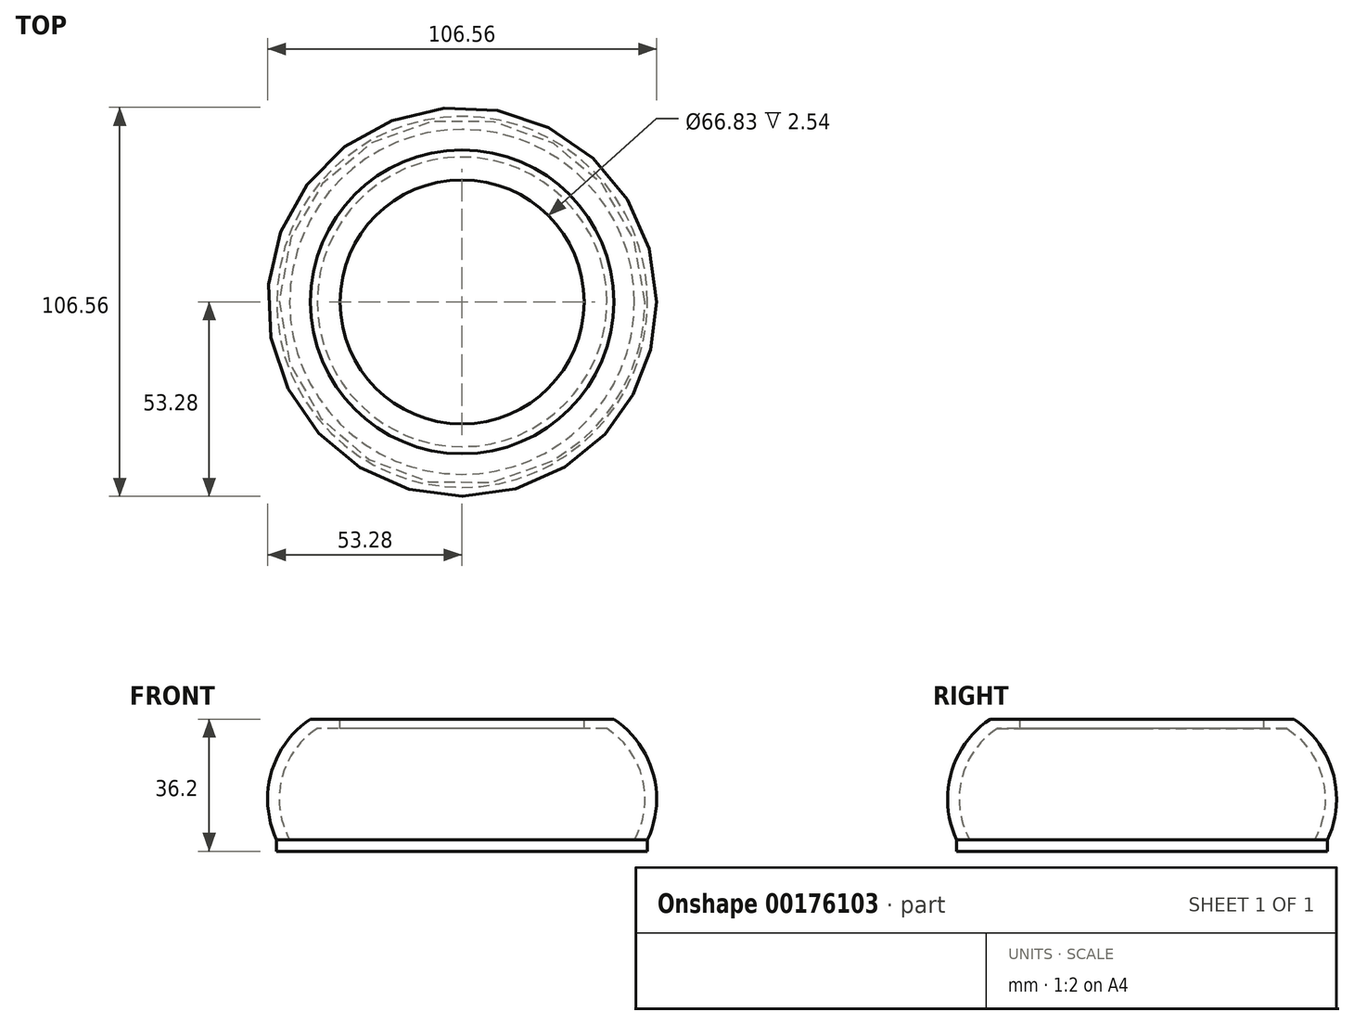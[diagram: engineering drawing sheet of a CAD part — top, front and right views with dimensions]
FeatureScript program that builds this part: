
annotation { "Feature Type Name" : "Feature", "Feature Type Description" : "" }
export const myFeature = defineFeature(function(context is Context, id is Id, definition is map)
    precondition{}
    {
        {
            var Q0;
            Q0=qCreatedBy(makeId("Front.planeOp"),FACE);
            var sketch = newSketch(context, id + "F0", { "sketchPlane" : qUnion([Q0])});
            skLineSegment(sketch, "E0", {"start": v(0, 0) * mm, "end": v(50.8, 0) * mm});
            skLineSegment(sketch, "E1", {"start": v(50.8, 0) * mm, "end": v(50.8, 3.18) * mm});
            skLineSegment(sketch, "E2", {"start": v(50.8, 3.18) * mm, "end": v(0, 3.17) * mm});
            skLineSegment(sketch, "E3", {"start": v(0, 3.17) * mm, "end": v(0, 0) * mm});
            skArc(sketch, "E4", {"start": v(50.8, 3.17) * mm, "mid": v(52.31, 21.4) * mm, "end": v(41.58, 36.2) * mm});
            skArc(sketch, "E5.0", {"start": v(47.24, 3.18) * mm, "mid": v(49.42, 19.9) * mm, "end": v(39.67, 33.65) * mm});
            skLineSegment(sketch, "E6", {"start": v(41.58, 36.2) * mm, "end": v(39.67, 33.65) * mm});
            skLineSegment(sketch, "E7", {"start": v(41.58, 36.2) * mm, "end": v(33.41, 36.2) * mm});
            skLineSegment(sketch, "E8", {"start": v(33.41, 36.2) * mm, "end": v(33.41, 33.66) * mm});
            skLineSegment(sketch, "E9", {"start": v(33.41, 33.66) * mm, "end": v(39.67, 33.66) * mm});
            skLineSegment(sketch, "E10", {"start": v(0, 40.5) * mm, "end": v(0, -31.39) * mm, "construction": true});
            skSolve(sketch);
        }
        {
            var Q0;
            Q0 = qSketchRegion(id + "F0", true);
            var Q1;
            Q1=sQuery(id+"F0.wireOp",EDGE,"E10");
            revolve(context, id + "F1", {"entities" : qUnion([Q0]), "axis" : qUnion([Q1]), "revolveType" : RevolveType.FULL});
        }
    });
